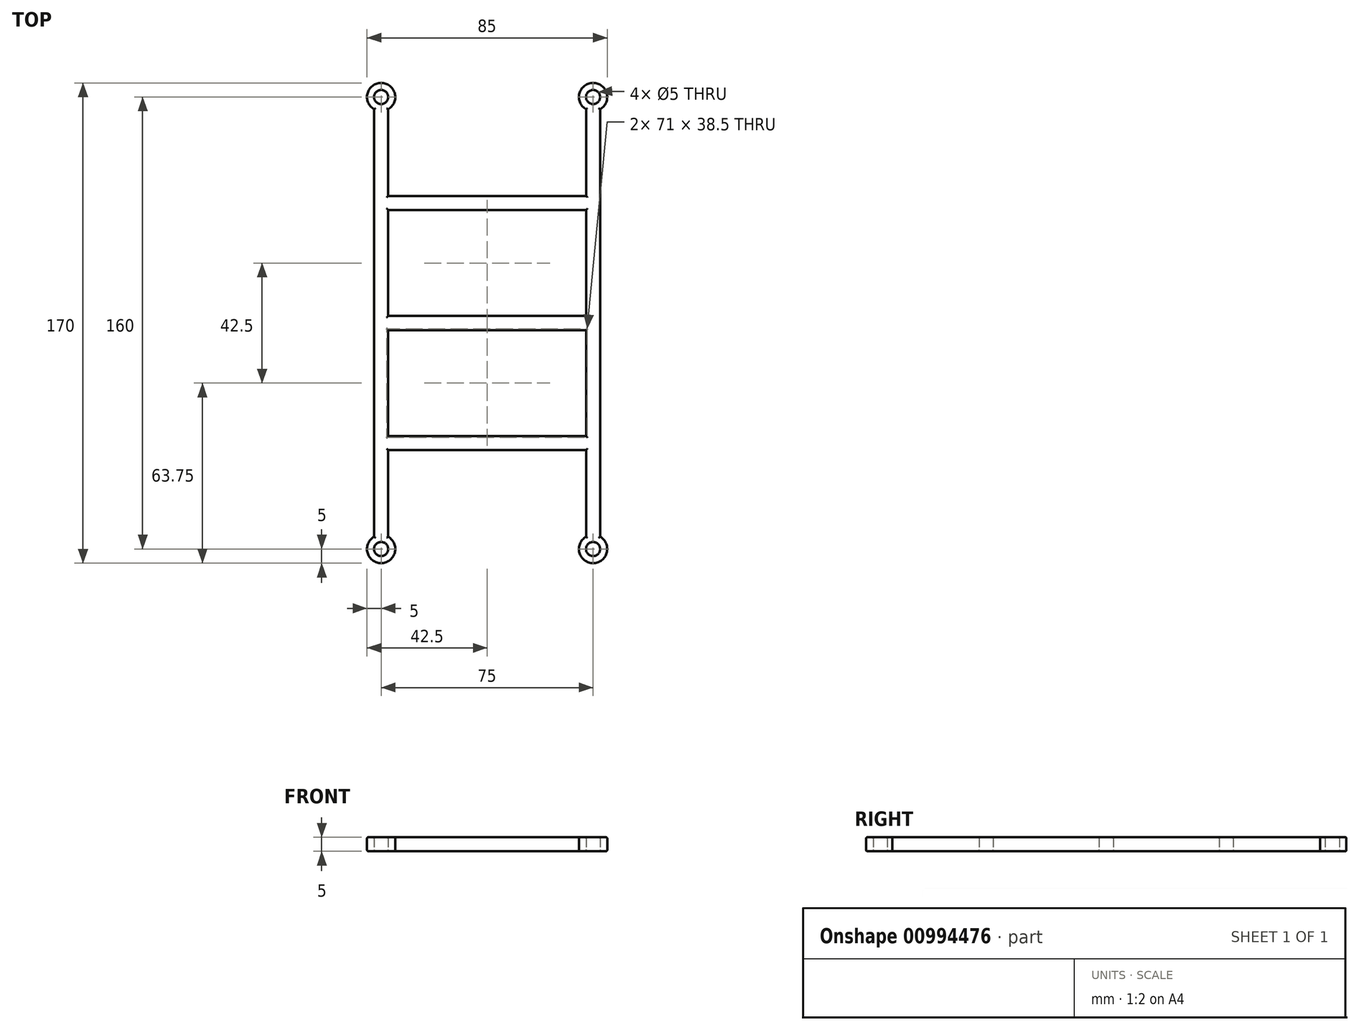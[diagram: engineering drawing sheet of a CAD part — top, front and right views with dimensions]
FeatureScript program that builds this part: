
annotation { "Feature Type Name" : "Feature", "Feature Type Description" : "" }
export const myFeature = defineFeature(function(context is Context, id is Id, definition is map)
    precondition{}
    {
        {
            assignVariable(context, id + "F0", {"name" : "winder_height", "anyValue" : 5});
        }
        {
            var Q0;
            Q0=qCreatedBy(makeId("Top.planeOp"),FACE);
            var sketch = newSketch(context, id + "F1", { "sketchPlane" : qUnion([Q0]), "disableImprinting" : false});
            skPoint(sketch, "E0.middle", {"position": v(0, 0) * mm});
            skLineSegment(sketch, "E1.bottom", {"start": v(0, 0) * mm, "end": v(40, 0) * mm});
            skLineSegment(sketch, "E1.left", {"start": v(0, 0) * mm, "end": v(0, 45) * mm});
            skLineSegment(sketch, "E1.right", {"start": v(40, 0) * mm, "end": v(40, 45) * mm});
            skLineSegment(sketch, "E2.bottom", {"start": v(40, 45) * mm, "end": v(35, 45) * mm, "construction": true});
            skLineSegment(sketch, "E3", {"start": v(0, 45) * mm, "end": v(35, 45) * mm});
            skLineSegment(sketch, "E4", {"start": v(40, 45) * mm, "end": v(40, 80) * mm});
            skLineSegment(sketch, "E5", {"start": v(40, 80) * mm, "end": v(35, 80) * mm});
            skLineSegment(sketch, "E6", {"start": v(35, 80) * mm, "end": v(35, 45) * mm});
            skLineSegment(sketch, "E7", {"start": v(37.5, 45) * mm, "end": v(37.5, 80) * mm, "construction": true});
            skCircle(sketch, "E8", {"center": v(37.5, 80) * mm, "radius": 2.5 * mm});
            skLineSegment(sketch, "E9.bottom", {"start": v(0, 40) * mm, "end": v(35, 40) * mm});
            skLineSegment(sketch, "E9.top", {"start": v(0, 2.5) * mm, "end": v(35, 2.5) * mm});
            skLineSegment(sketch, "E9.left", {"start": v(0, 40) * mm, "end": v(0, 2.5) * mm});
            skLineSegment(sketch, "E9.right", {"start": v(35, 40) * mm, "end": v(35, 2.5) * mm});
            skCircle(sketch, "E10", {"center": v(37.5, 80) * mm, "radius": 5 * mm});
            skSolve(sketch);
        }
        {
            var Q0;
            {var subQ7=sQuery(id+"F1.wireOp",EDGE,"E1.bottom");Q0=makeQuery(id+"F1.imprint","IMPRINT",FACE,{"disambiguationData":[TD([[makeQuery(id+"F1.imprint","IMPRINT",EDGE,{"derivedFrom":subQ7}),1.0]])]});}
            var Q1;
            {var subQ4=sQuery(id+"F1.wireOp",EDGE,"E10");var subQ6=sQuery(id+"F1.wireOp",EDGE,"E6");var subQ8=makeQuery(id+"F1.imprint","INTERSECT",VERTEX,{"derivedFrom":[subQ6,subQ4]});Q1=makeQuery(id+"F1.imprint","IMPRINT",FACE,{"disambiguationData":[TD([[makeQuery(id+"F1.imprint","IMPRINT",EDGE,{"disambiguationData":[TD([[subQ8,-1.0]])],"derivedFrom":subQ4}),1.0]])]});}
            var Q2;
            {var subQ4=sQuery(id+"F1.wireOp",EDGE,"E10");var subQ6=sQuery(id+"F1.wireOp",EDGE,"E6");var subQ7=makeQuery(id+"F1.imprint","INTERSECT",VERTEX,{"derivedFrom":[subQ6,subQ4]});Q2=makeQuery(id+"F1.imprint","IMPRINT",FACE,{"disambiguationData":[TD([[makeQuery(id+"F1.imprint","IMPRINT",EDGE,{"disambiguationData":[TD([[subQ7,1.0]])],"derivedFrom":subQ4}),1.0]])]});}
            var Q3;
            Q3=sQuery(id+"F1.wireOp",EDGE,"E2.bottom");
            extrude(context, id + "F2", {"entities" : qUnion([Q0, Q1, Q2]), "surfaceEntities" : qUnion([Q3]), "depth" : (getVariable(context, 'winder_height')) * mm, "offsetDistance" : 25 * mm});
        }
        {
            var Q0;
            Q0=makeQuery(id+"F2.opExtrude","SWEPT_BODY",BODY,{"disambiguationData":[OSD([sQuery(id+"F1.wireOp",EDGE,"E1.bottom"),sQuery(id+"F1.wireOp",EDGE,"E1.left"),sQuery(id+"F1.wireOp",EDGE,"E1.right"),sQuery(id+"F1.wireOp",EDGE,"E3"),sQuery(id+"F1.wireOp",EDGE,"E4"),sQuery(id+"F1.wireOp",EDGE,"E6"),sQuery(id+"F1.wireOp",EDGE,"E8"),sQuery(id+"F1.wireOp",EDGE,"E9.bottom"),sQuery(id+"F1.wireOp",EDGE,"E9.top"),sQuery(id+"F1.wireOp",EDGE,"E9.right"),sQuery(id+"F1.wireOp",EDGE,"E10")])]});
            var Q1;
            Q1=qCreatedBy(makeId("Front.planeOp"),FACE);
            mirror(context, id + "F3", {"operationType" : NewBodyOperationType.ADD, "entities" : qUnion([Q0]), "mirrorPlane" : qUnion([Q1])});
        }
        {
            var Q0;
            Q0=makeQuery(id+"F2.opExtrude","SWEPT_BODY",BODY,{"disambiguationData":[OSD([sQuery(id+"F1.wireOp",EDGE,"E1.bottom"),sQuery(id+"F1.wireOp",EDGE,"E1.left"),sQuery(id+"F1.wireOp",EDGE,"E1.right"),sQuery(id+"F1.wireOp",EDGE,"E3"),sQuery(id+"F1.wireOp",EDGE,"E4"),sQuery(id+"F1.wireOp",EDGE,"E6"),sQuery(id+"F1.wireOp",EDGE,"E8"),sQuery(id+"F1.wireOp",EDGE,"E9.bottom"),sQuery(id+"F1.wireOp",EDGE,"E9.top"),sQuery(id+"F1.wireOp",EDGE,"E9.right"),sQuery(id+"F1.wireOp",EDGE,"E10")])]});
            var Q1;
            Q1=qCreatedBy(makeId("Right.planeOp"),FACE);
            mirror(context, id + "F4", {"operationType" : NewBodyOperationType.ADD, "entities" : qUnion([Q0]), "mirrorPlane" : qUnion([Q1])});
        }
        {
            var Q0;
            {var subQ0=makeQuery(id+"F2.opExtrude","CAP_FACE",FACE,{"disambiguationData":[OSD([sQuery(id+"F1.wireOp",EDGE,"E1.bottom"),sQuery(id+"F1.wireOp",EDGE,"E1.left"),sQuery(id+"F1.wireOp",EDGE,"E1.right"),sQuery(id+"F1.wireOp",EDGE,"E3"),sQuery(id+"F1.wireOp",EDGE,"E4"),sQuery(id+"F1.wireOp",EDGE,"E6"),sQuery(id+"F1.wireOp",EDGE,"E8"),sQuery(id+"F1.wireOp",EDGE,"E9.bottom"),sQuery(id+"F1.wireOp",EDGE,"E9.top"),sQuery(id+"F1.wireOp",EDGE,"E9.right"),sQuery(id+"F1.wireOp",EDGE,"E10")])],"isStart":true});var subQ1=makeQuery(id+"F3.boolean.opBoolean","MERGE",FACE,{"derivedFrom":[subQ0,makeQuery(id+"F3.opPattern","COPY",FACE,{"derivedFrom":subQ0,"instanceName":"1"})]});Q0=makeQuery(id+"F4.boolean.opBoolean","MERGE",FACE,{"derivedFrom":[subQ1,makeQuery(id+"F4.opPattern","COPY",FACE,{"derivedFrom":subQ1,"instanceName":"1"})]});}
            var Q1;
            {var subQ0=makeQuery(id+"F2.opExtrude","CAP_FACE",FACE,{"disambiguationData":[OSD([sQuery(id+"F1.wireOp",EDGE,"E1.bottom"),sQuery(id+"F1.wireOp",EDGE,"E1.left"),sQuery(id+"F1.wireOp",EDGE,"E1.right"),sQuery(id+"F1.wireOp",EDGE,"E3"),sQuery(id+"F1.wireOp",EDGE,"E4"),sQuery(id+"F1.wireOp",EDGE,"E6"),sQuery(id+"F1.wireOp",EDGE,"E8"),sQuery(id+"F1.wireOp",EDGE,"E9.bottom"),sQuery(id+"F1.wireOp",EDGE,"E9.top"),sQuery(id+"F1.wireOp",EDGE,"E9.right"),sQuery(id+"F1.wireOp",EDGE,"E10")])],"isStart":false});var subQ1=makeQuery(id+"F3.boolean.opBoolean","MERGE",FACE,{"derivedFrom":[subQ0,makeQuery(id+"F3.opPattern","COPY",FACE,{"derivedFrom":subQ0,"instanceName":"1"})]});Q1=makeQuery(id+"F4.boolean.opBoolean","MERGE",FACE,{"derivedFrom":[subQ1,makeQuery(id+"F4.opPattern","COPY",FACE,{"derivedFrom":subQ1,"instanceName":"1"})]});}
            fillet(context, id + "F5", {"entities" : qUnion([Q0, Q1]), "radius" : 0.5 * mm, "tangentPropagation" : true, "allowEdgeOverflow" : false});
        }
    });
